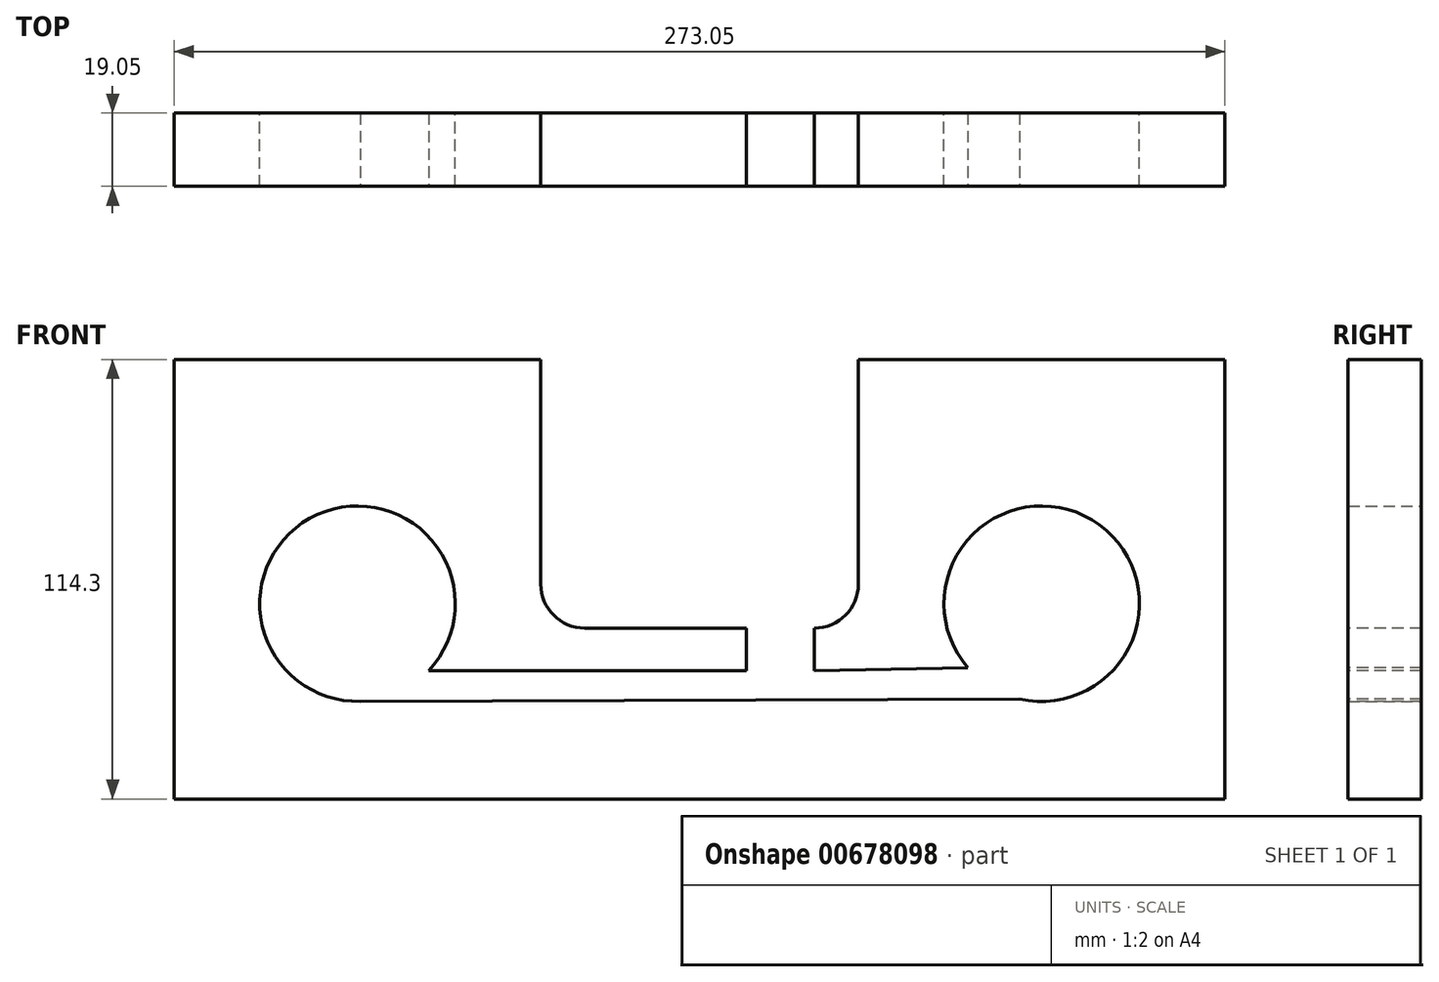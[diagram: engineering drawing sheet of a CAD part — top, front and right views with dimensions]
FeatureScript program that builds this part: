
annotation { "Feature Type Name" : "Feature", "Feature Type Description" : "" }
export const myFeature = defineFeature(function(context is Context, id is Id, definition is map)
    precondition{}
    {
        {
            var Q0;
            Q0=qCreatedBy(makeId("Front.planeOp"),FACE);
            var sketch = newSketch(context, id + "F0", { "sketchPlane" : qUnion([Q0])});
            skLineSegment(sketch, "E0.bottom", {"start": v(0, 0) * mm, "end": v(273.05, 0) * mm});
            skLineSegment(sketch, "E0.top", {"start": v(0, 114.3) * mm, "end": v(273.05, 114.3) * mm});
            skLineSegment(sketch, "E0.left", {"start": v(0, 0) * mm, "end": v(0, 114.3) * mm});
            skLineSegment(sketch, "E0.right", {"start": v(273.05, 0) * mm, "end": v(273.05, 114.3) * mm});
            skCircle(sketch, "E1", {"center": v(47.62, 50.8) * mm, "radius": 25.4 * mm});
            skCircle(sketch, "E2", {"center": v(225.42, 50.8) * mm, "radius": 25.4 * mm});
            skSolve(sketch);
        }
        {
            var Q0;
            Q0=makeQuery(id+"F0.imprint","IMPRINT",FACE,{"disambiguationData":[TD([[makeQuery(id+"F0.imprint","IMPRINT",EDGE,{"derivedFrom":sQuery(id+"F0.wireOp",EDGE,"E0.bottom")}),1.0]])]});
            extrude(context, id + "F1", {"entities" : qUnion([Q0]), "depth" : 19.05 * mm, "offsetDistance" : 25.4 * mm});
        }
        {
            var Q0;
            Q0=makeQuery(id+"F1.opExtrude","CAP_FACE",FACE,{"disambiguationData":[OSD([sQuery(id+"F0.wireOp",EDGE,"E0.bottom"),sQuery(id+"F0.wireOp",EDGE,"E0.top"),sQuery(id+"F0.wireOp",EDGE,"E0.left"),sQuery(id+"F0.wireOp",EDGE,"E0.right"),sQuery(id+"F0.wireOp",EDGE,"E1"),sQuery(id+"F0.wireOp",EDGE,"E2")])],"isStart":false});
            var sketch = newSketch(context, id + "F2", { "sketchPlane" : qUnion([Q0])});
            skLineSegment(sketch, "E3", {"start": v(95.25, 114.3) * mm, "end": v(95.25, 55.88) * mm});
            skLineSegment(sketch, "E4", {"start": v(106.68, 44.45) * mm, "end": v(166.37, 44.45) * mm});
            skLineSegment(sketch, "E5", {"start": v(177.8, 55.88) * mm, "end": v(177.8, 114.3) * mm});
            skPoint(sketch, "E6.visualSharp", {"position": v(95.25, 44.45) * mm});
            skArc(sketch, "E6.filletArc", {"start": v(95.25, 55.88) * mm, "mid": v(98.6, 47.8) * mm, "end": v(106.68, 44.45) * mm});
            skPoint(sketch, "E7.visualSharp", {"position": v(177.8, 44.45) * mm});
            skArc(sketch, "E7.filletArc", {"start": v(166.37, 44.45) * mm, "mid": v(174.45, 47.8) * mm, "end": v(177.8, 55.88) * mm});
            skSolve(sketch);
        }
        {
            var Q0;
            Q0 = qSketchRegion(id + "F2", true);
            var Q1;
            {var subQ1=sQuery(id+"F2.wireOp",EDGE,"E3");Q1=makeQuery(id+"F2.imprint","IMPRINT",FACE,{"disambiguationData":[TD([[makeQuery(id+"F2.imprint","IMPRINT",EDGE,{"derivedFrom":subQ1}),1.0]])]});}
            extrude(context, id + "F3", {"entities" : qUnion([Q0, Q1]), "operationType" : NewBodyOperationType.REMOVE, "oppositeDirection" : true, "depth" : 25.4 * mm, "offsetDistance" : 25.4 * mm});
        }
        {
            var Q0;
            Q0=makeQuery(id+"F1.opExtrude","CAP_FACE",FACE,{"disambiguationData":[OSD([sQuery(id+"F0.wireOp",EDGE,"E0.bottom"),sQuery(id+"F0.wireOp",EDGE,"E0.top"),sQuery(id+"F0.wireOp",EDGE,"E0.left"),sQuery(id+"F0.wireOp",EDGE,"E0.right"),sQuery(id+"F0.wireOp",EDGE,"E1"),sQuery(id+"F0.wireOp",EDGE,"E2")])],"isStart":false});
            var sketch = newSketch(context, id + "F4", { "sketchPlane" : qUnion([Q0])});
            skLineSegment(sketch, "E8", {"start": v(166.37, 44.45) * mm, "end": v(148.62, 44.45) * mm});
            skLineSegment(sketch, "E9", {"start": v(148.62, 44.45) * mm, "end": v(148.62, 33.36) * mm});
            skLineSegment(sketch, "E10", {"start": v(148.62, 33.36) * mm, "end": v(66.1, 33.36) * mm});
            skLineSegment(sketch, "E11", {"start": v(66.1, 33.36) * mm, "end": v(47.03, 25.4) * mm});
            skLineSegment(sketch, "E12", {"start": v(47.03, 25.4) * mm, "end": v(219.74, 26.05) * mm});
            skLineSegment(sketch, "E13", {"start": v(219.74, 26.05) * mm, "end": v(206.23, 34.16) * mm});
            skLineSegment(sketch, "E14", {"start": v(206.23, 34.16) * mm, "end": v(166.37, 33.36) * mm});
            skLineSegment(sketch, "E15", {"start": v(166.37, 33.36) * mm, "end": v(166.37, 44.45) * mm});
            skSolve(sketch);
        }
        {
            var Q0;
            Q0=makeQuery(id+"F4.imprint","IMPRINT",FACE,{"disambiguationData":[TD([[makeQuery(id+"F4.imprint","IMPRINT",EDGE,{"derivedFrom":sQuery(id+"F4.wireOp",EDGE,"E8")}),-1.0]])]});
            extrude(context, id + "F5", {"entities" : qUnion([Q0]), "operationType" : NewBodyOperationType.REMOVE, "oppositeDirection" : true, "depth" : 25.4 * mm, "offsetDistance" : 25.4 * mm});
        }
    });
